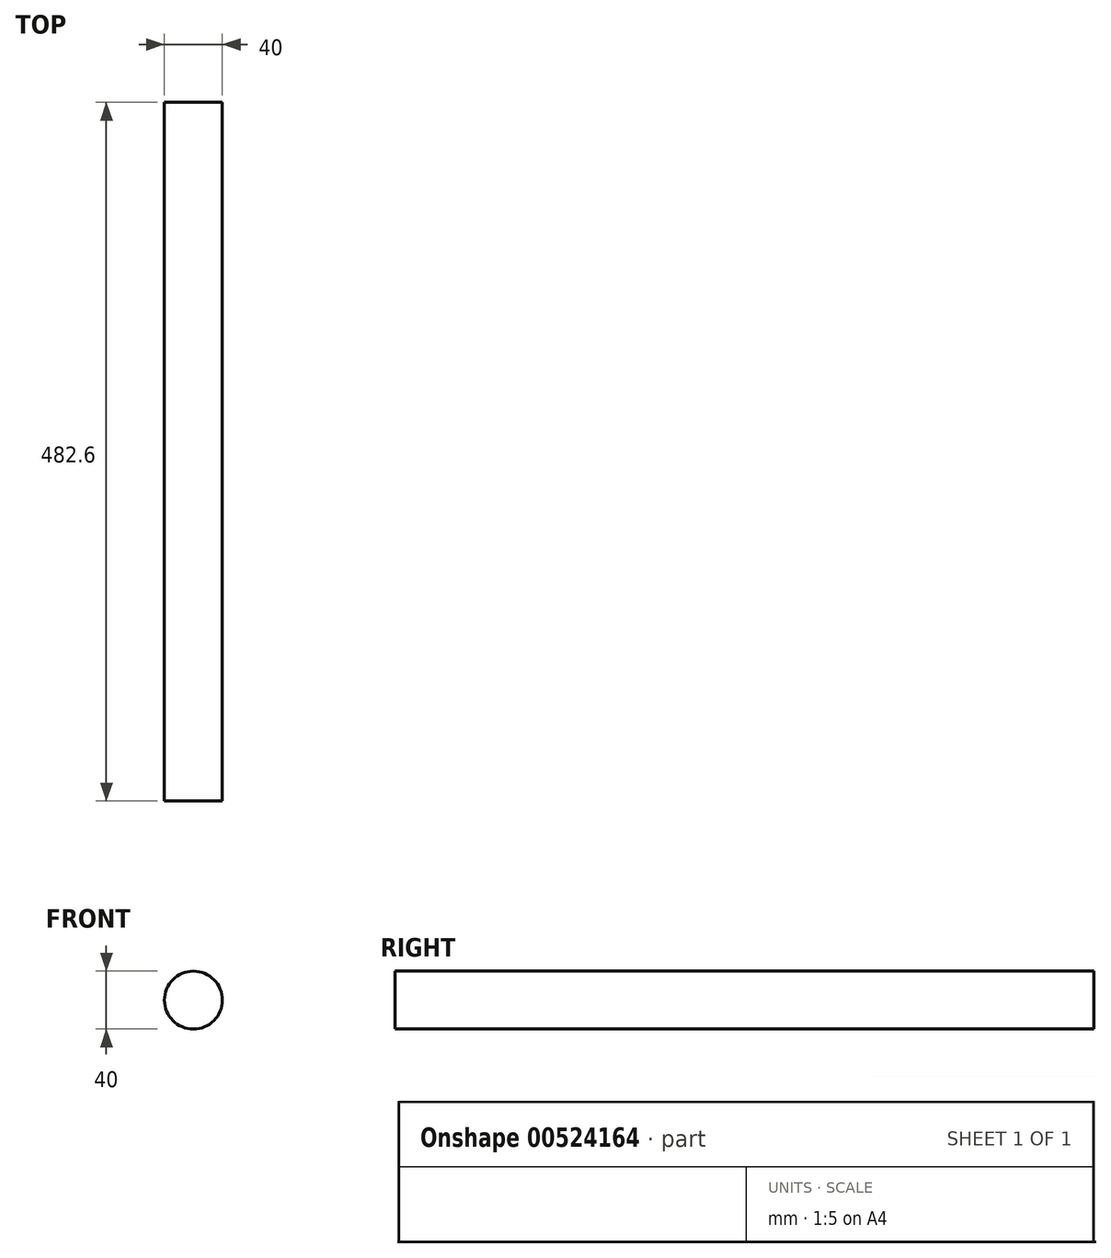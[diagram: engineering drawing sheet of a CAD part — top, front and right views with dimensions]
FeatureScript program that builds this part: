
annotation { "Feature Type Name" : "Feature", "Feature Type Description" : "" }
export const myFeature = defineFeature(function(context is Context, id is Id, definition is map)
    precondition{}
    {
        {
            var Q0;
            Q0=qCreatedBy(makeId("Front.planeOp"),FACE);
            var sketch = newSketch(context, id + "F0", { "sketchPlane" : qUnion([Q0])});
            skCircle(sketch, "E0", {"center": v(0, 0) * mm, "radius": 20 * mm});
            skSolve(sketch);
        }
        {
            var Q0;
            Q0=qSketchRegion(id+"F0",true);
            extrude(context, id + "F1", {"entities" : qUnion([Q0]), "endBound" : BoundingType.SYMMETRIC, "depth" : 482.6 * mm});
        }
    });
